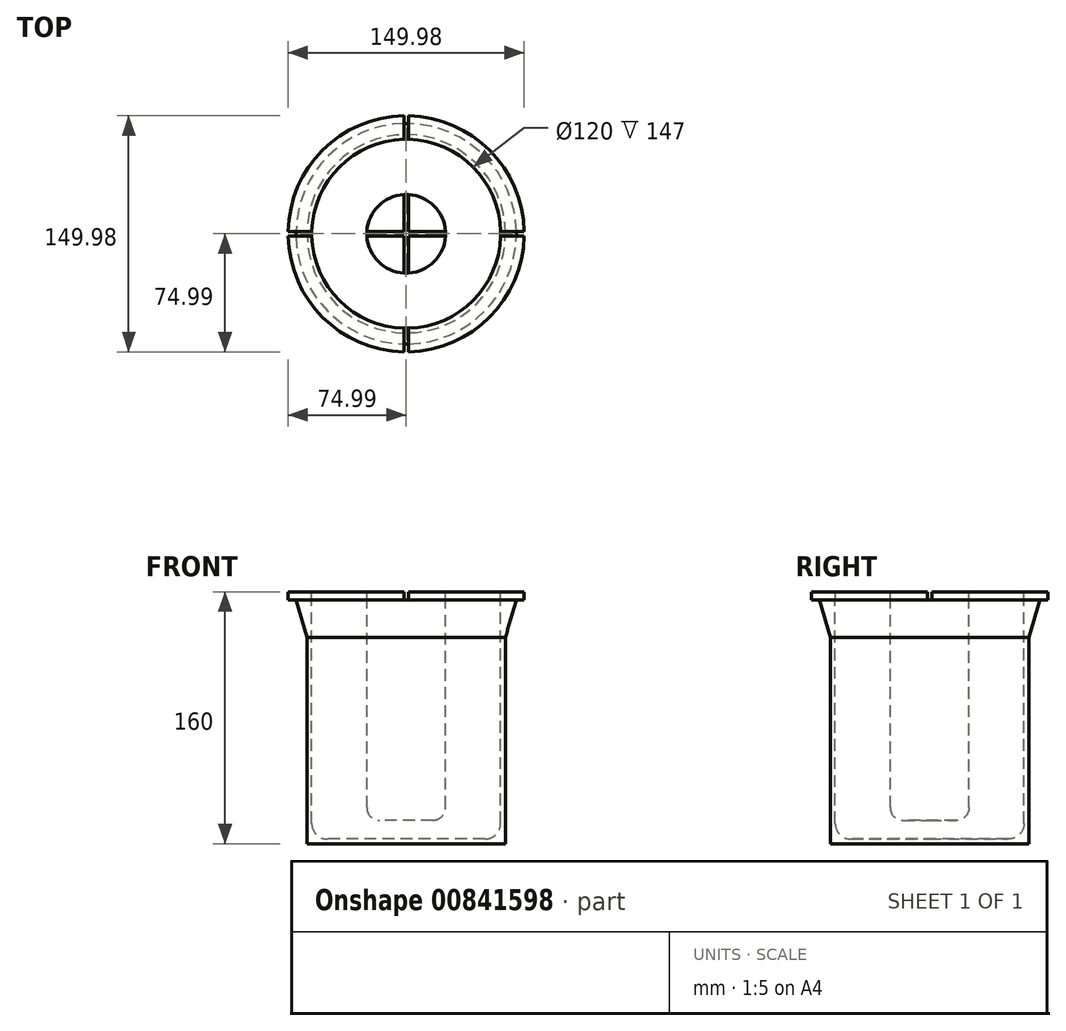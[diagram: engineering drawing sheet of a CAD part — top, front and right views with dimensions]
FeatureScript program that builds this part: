
annotation { "Feature Type Name" : "Feature", "Feature Type Description" : "" }
export const myFeature = defineFeature(function(context is Context, id is Id, definition is map)
    precondition{}
    {
        {
            var Q0;
            Q0=qCreatedBy(makeId("Front.planeOp"),FACE);
            var sketch = newSketch(context, id + "F0", { "sketchPlane" : qUnion([Q0])});
            skLineSegment(sketch, "E0", {"start": v(-185.35, 0) * mm, "end": v(260.33, 0) * mm, "construction": true});
            skLineSegment(sketch, "E1", {"start": v(-182.18, 160) * mm, "end": v(207.52, 160) * mm, "construction": true});
            skLineSegment(sketch, "E2", {"start": v(0, 15) * mm, "end": v(17, 15) * mm});
            skLineSegment(sketch, "E3", {"start": v(25, 23) * mm, "end": v(25, 160) * mm});
            skLineSegment(sketch, "E4", {"start": v(25, 160) * mm, "end": v(0, 160) * mm});
            skLineSegment(sketch, "E5", {"start": v(0, 160) * mm, "end": v(0, 15) * mm});
            skPoint(sketch, "E6.visualSharp", {"position": v(25, 15) * mm});
            skArc(sketch, "E6.filletArc", {"start": v(17, 15) * mm, "mid": v(22.66, 17.34) * mm, "end": v(25, 23) * mm});
            skSolve(sketch);
        }
        {
            var Q0;
            Q0=makeQuery(id+"F0.imprint","IMPRINT",FACE,{"disambiguationData":[TD([[makeQuery(id+"F0.imprint","IMPRINT",EDGE,{"derivedFrom":sQuery(id+"F0.wireOp",EDGE,"E2")}),1.0]])]});
            var Q1;
            Q1=sQuery(id+"F0.wireOp",EDGE,"E5");
            revolve(context, id + "F1", {"surfaceOperationType" : NewSurfaceOperationType.NEW, "entities" : qUnion([Q0]), "axis" : qUnion([Q1]), "revolveType" : RevolveType.FULL});
        }
        {
            var Q0;
            Q0=qCreatedBy(makeId("Top.planeOp"),FACE);
            cPlane(context, id + "F2", {"entities" : qUnion([Q0]), "cplaneType" : CPlaneType.OFFSET, "offset" : 160 * mm, "width" : 150 * mm, "height" : 150 * mm});
        }
        {
            var Q0;
            Q0=qCreatedBy(id+"F2.planeOp",FACE);
            var sketch = newSketch(context, id + "F3", { "sketchPlane" : qUnion([Q0])});
            skLineSegment(sketch, "E7.0", {"start": v(-77.44, -1.55) * mm, "end": v(77.56, -1.55) * mm});
            skLineSegment(sketch, "E8.0", {"start": v(-77.44, 1.45) * mm, "end": v(77.56, 1.45) * mm});
            skLineSegment(sketch, "E9", {"start": v(-77.44, -1.55) * mm, "end": v(-77.44, 1.45) * mm});
            skLineSegment(sketch, "E10", {"start": v(77.56, -1.55) * mm, "end": v(77.56, 1.45) * mm});
            skLineSegment(sketch, "E11.bottom", {"start": v(-1.46, 77.78) * mm, "end": v(1.54, 77.78) * mm});
            skLineSegment(sketch, "E11.top", {"start": v(-1.46, -77.22) * mm, "end": v(1.54, -77.22) * mm});
            skLineSegment(sketch, "E11.left", {"start": v(-1.46, 77.78) * mm, "end": v(-1.46, -77.22) * mm});
            skLineSegment(sketch, "E11.right", {"start": v(1.54, 77.78) * mm, "end": v(1.54, -77.22) * mm});
            skCircle(sketch, "E12.0", {"center": v(0, 0) * mm, "radius": 25 * mm});
            skLineSegment(sketch, "E13.0", {"start": v(1.5, 29.6) * mm, "end": v(1.5, -29.89) * mm, "construction": true});
            skLineSegment(sketch, "E14.0", {"start": v(-1.5, 29.6) * mm, "end": v(-1.5, -29.89) * mm, "construction": true});
            skLineSegment(sketch, "E15.0", {"start": v(-28.5, -1.5) * mm, "end": v(30.98, -1.5) * mm, "construction": true});
            skLineSegment(sketch, "E16.0", {"start": v(-28.5, 1.5) * mm, "end": v(30.98, 1.5) * mm, "construction": true});
            skSolve(sketch);
        }
        {
            var Q0;
            Q0 = qSketchRegion(id + "F3", true);
            extrude(context, id + "F4", {"entities" : qUnion([Q0]), "operationType" : NewBodyOperationType.ADD, "oppositeDirection" : true, "depth" : 5 * mm, "offsetDistance" : 25 * mm});
        }
        {
            var Q0;
            Q0=qCreatedBy(makeId("Front.planeOp"),FACE);
            var sketch = newSketch(context, id + "F5", { "sketchPlane" : qUnion([Q0])});
            skLineSegment(sketch, "E17", {"start": v(0, 0) * mm, "end": v(63, 0) * mm});
            skLineSegment(sketch, "E18", {"start": v(63, 0) * mm, "end": v(63, 131) * mm});
            skLineSegment(sketch, "E19", {"start": v(63, 131) * mm, "end": v(70, 155) * mm});
            skLineSegment(sketch, "E20", {"start": v(70, 155) * mm, "end": v(75, 155) * mm});
            skLineSegment(sketch, "E21", {"start": v(75, 155) * mm, "end": v(75, 160) * mm});
            skLineSegment(sketch, "E22", {"start": v(75, 160) * mm, "end": v(60, 160) * mm});
            skLineSegment(sketch, "E23", {"start": v(60, 160) * mm, "end": v(60, 13) * mm});
            skLineSegment(sketch, "E24", {"start": v(50, 3) * mm, "end": v(0, 3) * mm});
            skLineSegment(sketch, "E25", {"start": v(0, 3) * mm, "end": v(0, 0) * mm});
            skPoint(sketch, "E26.visualSharp", {"position": v(60, 3) * mm});
            skArc(sketch, "E26.filletArc", {"start": v(50, 3) * mm, "mid": v(57.07, 5.93) * mm, "end": v(60, 13) * mm});
            skSolve(sketch);
        }
        {
            var Q0;
            Q0=makeQuery(id+"F5.imprint","IMPRINT",FACE,{"disambiguationData":[TD([[makeQuery(id+"F5.imprint","IMPRINT",EDGE,{"derivedFrom":sQuery(id+"F5.wireOp",EDGE,"E17")}),1.0]])]});
            var Q1;
            Q1=sQuery(id+"F5.wireOp",EDGE,"E25");
            revolve(context, id + "F6", {"surfaceOperationType" : NewSurfaceOperationType.NEW, "entities" : qUnion([Q0]), "axis" : qUnion([Q1]), "revolveType" : RevolveType.FULL});
        }
        {
            var Q0;
            Q0=makeQuery(id+"F4.opExtrude","SWEPT_FACE",FACE,{"disambiguationData":[OSD([sQuery(id+"F3.wireOp",EDGE,"E11.top")])]});
            extrude(context, id + "F7", {"entities" : qUnion([Q0]), "operationType" : NewBodyOperationType.REMOVE, "endBound" : BoundingType.THROUGH_ALL, "oppositeDirection" : true, "depth" : 25 * mm, "offsetDistance" : 25 * mm});
        }
        {
            var Q0;
            Q0=makeQuery(id+"F4.opExtrude","SWEPT_FACE",FACE,{"disambiguationData":[OSD([sQuery(id+"F3.wireOp",EDGE,"E9")])]});
            extrude(context, id + "F8", {"entities" : qUnion([Q0]), "operationType" : NewBodyOperationType.REMOVE, "endBound" : BoundingType.THROUGH_ALL, "oppositeDirection" : true, "depth" : 25 * mm, "offsetDistance" : 25 * mm});
        }
    });
